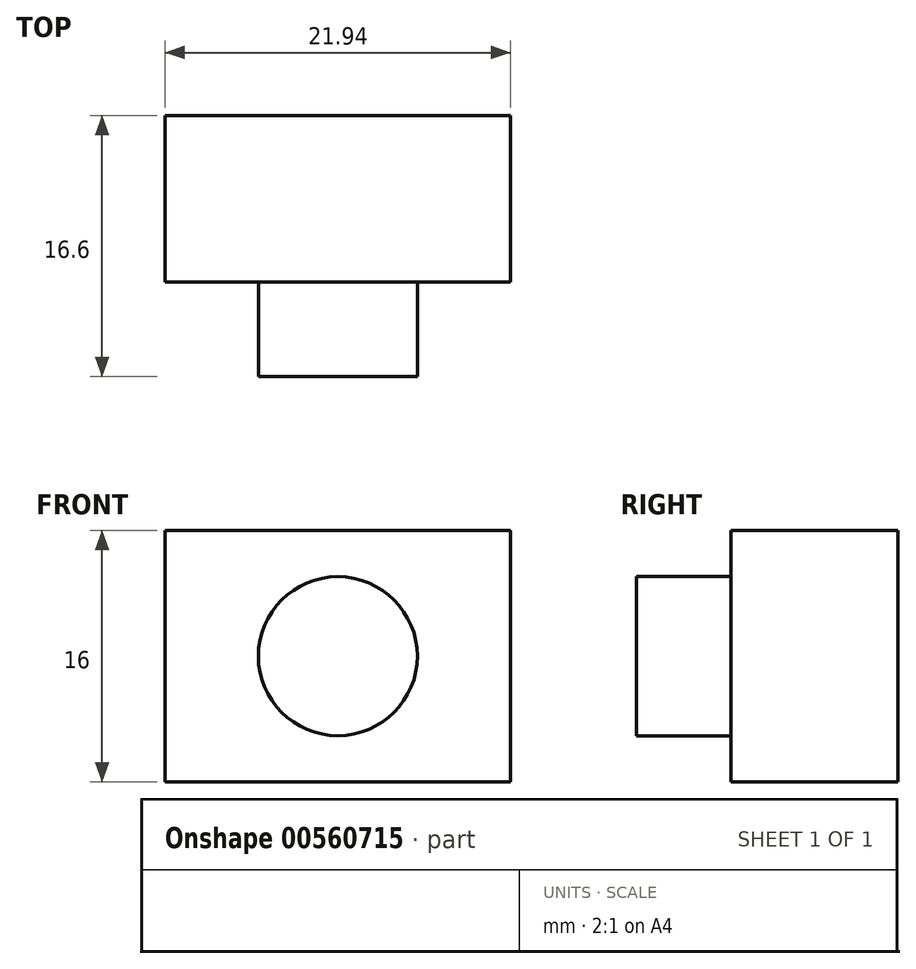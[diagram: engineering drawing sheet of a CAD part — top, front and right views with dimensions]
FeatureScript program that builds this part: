
annotation { "Feature Type Name" : "Feature", "Feature Type Description" : "" }
export const myFeature = defineFeature(function(context is Context, id is Id, definition is map)
    precondition{}
    {
        {
            var Q0;
            Q0=qCreatedBy(makeId("Front.planeOp"),FACE);
            var sketch = newSketch(context, id + "F0", { "sketchPlane" : qUnion([Q0])});
            skLineSegment(sketch, "E0.bottom", {"start": v(10.97, 0) * mm, "end": v(-10.97, 0) * mm});
            skLineSegment(sketch, "E0.top", {"start": v(10.97, 16) * mm, "end": v(-10.98, 16) * mm});
            skLineSegment(sketch, "E0.left", {"start": v(10.97, 0) * mm, "end": v(10.97, 16) * mm});
            skLineSegment(sketch, "E0.right", {"start": v(-10.97, 0) * mm, "end": v(-10.97, 16) * mm});
            skPoint(sketch, "E1", {"position": v(0, 0) * mm});
            skPoint(sketch, "E2", {"position": v(0, 8) * mm});
            skCircle(sketch, "E3", {"center": v(0, 8) * mm, "radius": 5.05 * mm});
            skSolve(sketch);
        }
        {
            var Q0;
            Q0=makeQuery(id+"F0.imprint","IMPRINT",FACE,{"disambiguationData":[TD([[makeQuery(id+"F0.imprint","IMPRINT",EDGE,{"derivedFrom":sQuery(id+"F0.wireOp",EDGE,"E3")}),1.0]])]});
            extrude(context, id + "F1", {"entities" : qUnion([Q0]), "depth" : 6 * mm, "offsetDistance" : 25 * mm});
        }
        {
            var Q0;
            Q0=makeQuery(id+"F0.imprint","IMPRINT",FACE,{"disambiguationData":[TD([[makeQuery(id+"F0.imprint","IMPRINT",EDGE,{"derivedFrom":sQuery(id+"F0.wireOp",EDGE,"E0.bottom")}),-1.0]])]});
            var Q1;
            Q1=makeQuery(id+"F0.imprint","IMPRINT",FACE,{"disambiguationData":[TD([[makeQuery(id+"F0.imprint","IMPRINT",EDGE,{"derivedFrom":sQuery(id+"F0.wireOp",EDGE,"E3")}),1.0]])]});
            extrude(context, id + "F2", {"entities" : qUnion([Q0, Q1]), "operationType" : NewBodyOperationType.ADD, "oppositeDirection" : true, "depth" : 10.6 * mm, "offsetDistance" : 25 * mm});
        }
    });
